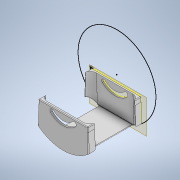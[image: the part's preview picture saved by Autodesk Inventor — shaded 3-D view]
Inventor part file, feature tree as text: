
AUTODESK INVENTOR PART (.ipt)
format: ipt  version: 2022 (Build 260153000, 153)  size: 564,736 bytes
history: native  units: mm
features: reference x23, other x10, sketch x6, extrude x4, fillet x4, projected_geometry x4, mirror x1, loft x1
ambient origin geometry x8: Origin, YZ Plane, XZ Plane, XY Plane, X Axis, Y Axis, Z Axis, Center Point
bodies: Body1 (feature_tree)
feature tree (53):
  other  "Твердое тело1"
  other  "РабПлоскость1"
  other  "РабПлоскость2"
  extrude  "Выдавливание1"  Depth=0.12mm
  other  "РабПлоскость3"
  extrude  "Выдавливание5"  Depth=10.0mm TaperAngle=0.0deg
  extrude  "Выдавливание6"  Depth=0.3mm
  sketch  "Эскиз10"
  fillet  "Сопряжение5"  Radius=10.0mm
  mirror  "Зеркальное отражение2"
  extrude  "Выдавливание8"  Depth=5.0mm TaperAngle=0.0deg
  loft  "Лофт3"
  fillet  "Сопряжение7"  Radius=0.12mm
  fillet  "Сопряжение8"  Radius=50.0mm
  fillet  "Сопряжение9"  [1 undecoded]
  sketch  "Эскиз13"
  reference  "Ссылка1"
  reference  "Ссылка2"
  reference  "Ссылка3"
  reference  "Ссылка4"
  reference  "Ссылка5"
  reference  "Ссылка6"
  reference  "Ссылка7"
  reference  "Ссылка8"
  reference  "Ссылка9"
  reference  "Ссылка10"
  reference  "Ссылка11"
  sketch  "Эскиз8"
  projected_geometry  "Спроецированная петля4"
  reference  "Ссылка28"
  sketch  "Эскиз9"
  projected_geometry  "Спроецированная петля5"
  projected_geometry  "Спроецированная петля6"
  reference  "Ссылка29"
  sketch  "Эскиз11"
  reference  "Ссылка31"
  sketch  "Эскиз12"
  reference  "Ссылка32"
  reference  "Ссылка38"
  reference  "Ссылка41"
  reference  "Ссылка42"
  reference  "Ссылка43"
  reference  "Ссылка44"
  reference  "Ссылка45"
  reference  "Ссылка46"
  reference  "Ссылка47"
  projected_geometry  "Спроецированная петля7"
  other  "<userpath>\Documents\Git\MZCAT_2024\MZCAT_4.iam"
  other  "MZCAT_4.iam"
  other  "lidar_krestovina:1"
  other  "LD19:1"
  other  "<userpath>\Documents\Git\MZCAT_2024\MZCAT_3.iam"
  other  "MZCAT_3.iam"
note: 1 required parameter value undecoded (feature->parameter linkage not recoverable at this tier; creation-order binding heuristic only, values carry confidence <= 0.55)
